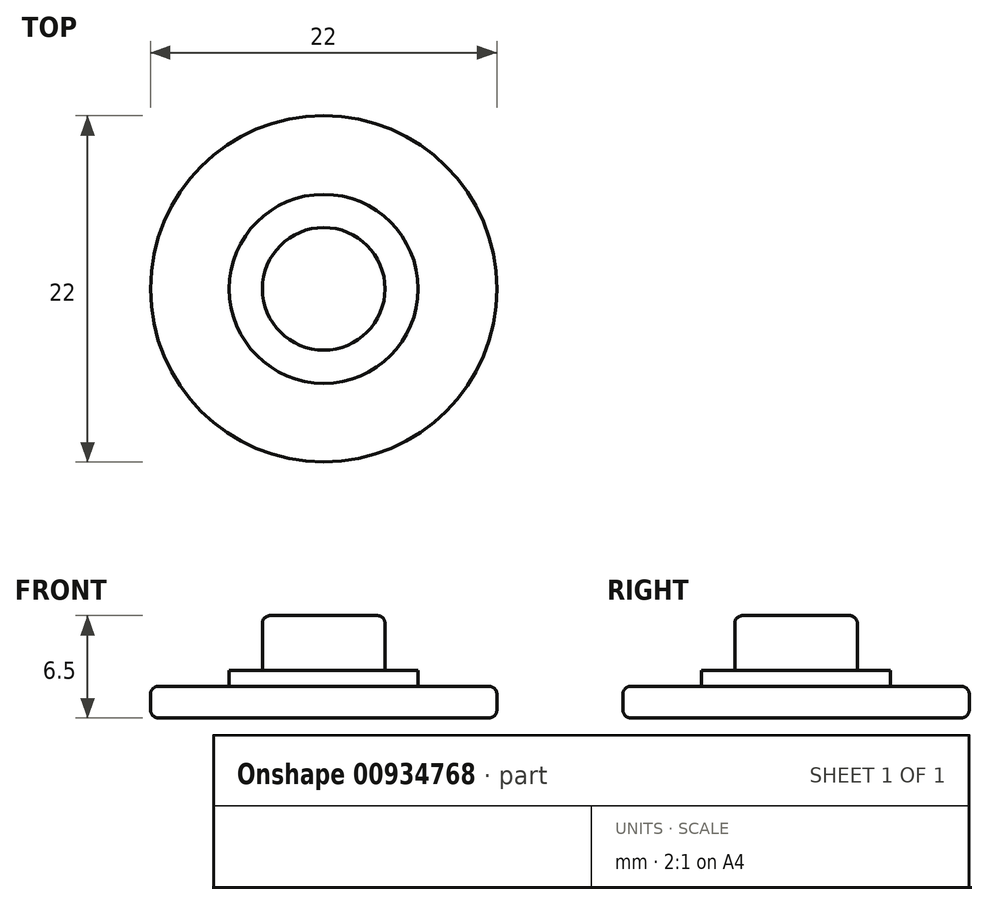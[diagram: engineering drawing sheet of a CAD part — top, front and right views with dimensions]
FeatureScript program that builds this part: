
annotation { "Feature Type Name" : "Feature", "Feature Type Description" : "" }
export const myFeature = defineFeature(function(context is Context, id is Id, definition is map)
    precondition{}
    {
        {
            var Q0;
            Q0=qCreatedBy(makeId("Top.planeOp"),FACE);
            var sketch = newSketch(context, id + "F0", { "sketchPlane" : qUnion([Q0])});
            skCircle(sketch, "E0", {"center": v(0, 0) * mm, "radius": 11 * mm});
            skCircle(sketch, "E1", {"center": v(0, 0) * mm, "radius": 6 * mm});
            skCircle(sketch, "E2", {"center": v(0, 0) * mm, "radius": 3.9 * mm});
            skSolve(sketch);
        }
        {
            var Q0;
            Q0=makeQuery(id+"F0.imprint","IMPRINT",FACE,{"disambiguationData":[TD([[makeQuery(id+"F0.imprint","IMPRINT",EDGE,{"derivedFrom":sQuery(id+"F0.wireOp",EDGE,"E0")}),1.0]])]});
            extrude(context, id + "F1", {"entities" : qUnion([Q0]), "depth" : 2 * mm, "offsetDistance" : 25 * mm});
        }
        {
            var Q0;
            Q0=makeQuery(id+"F0.imprint","IMPRINT",FACE,{"disambiguationData":[TD([[makeQuery(id+"F0.imprint","IMPRINT",EDGE,{"derivedFrom":sQuery(id+"F0.wireOp",EDGE,"E1")}),1.0]])]});
            extrude(context, id + "F2", {"entities" : qUnion([Q0]), "operationType" : NewBodyOperationType.ADD, "depth" : 3 * mm, "offsetDistance" : 25 * mm});
        }
        {
            var Q0;
            Q0=makeQuery(id+"F0.imprint","IMPRINT",FACE,{"disambiguationData":[TD([[makeQuery(id+"F0.imprint","IMPRINT",EDGE,{"derivedFrom":sQuery(id+"F0.wireOp",EDGE,"E2")}),1.0]])]});
            extrude(context, id + "F3", {"entities" : qUnion([Q0]), "operationType" : NewBodyOperationType.ADD, "depth" : 6.5 * mm, "offsetDistance" : 25 * mm});
        }
        {
            var Q0;
            Q0=makeQuery(id+"F3.opExtrude","CAP_EDGE",EDGE,{"disambiguationData":[OSD([sQuery(id+"F0.wireOp",EDGE,"E2")])],"isStart":false});
            fillet(context, id + "F4", {"entities" : qUnion([Q0]), "radius" : 0.5 * mm, "tangentPropagation" : true, "allowEdgeOverflow" : false});
        }
        {
            var Q0;
            Q0=makeQuery(id+"F1.opExtrude","CAP_EDGE",EDGE,{"disambiguationData":[OSD([sQuery(id+"F0.wireOp",EDGE,"E0")])],"isStart":true});
            var Q1;
            Q1=makeQuery(id+"F1.opExtrude","CAP_EDGE",EDGE,{"disambiguationData":[OSD([sQuery(id+"F0.wireOp",EDGE,"E0")])],"isStart":false});
            fillet(context, id + "F5", {"entities" : qUnion([Q0, Q1]), "radius" : .5 * mm, "tangentPropagation" : true, "allowEdgeOverflow" : false});
        }
    });
